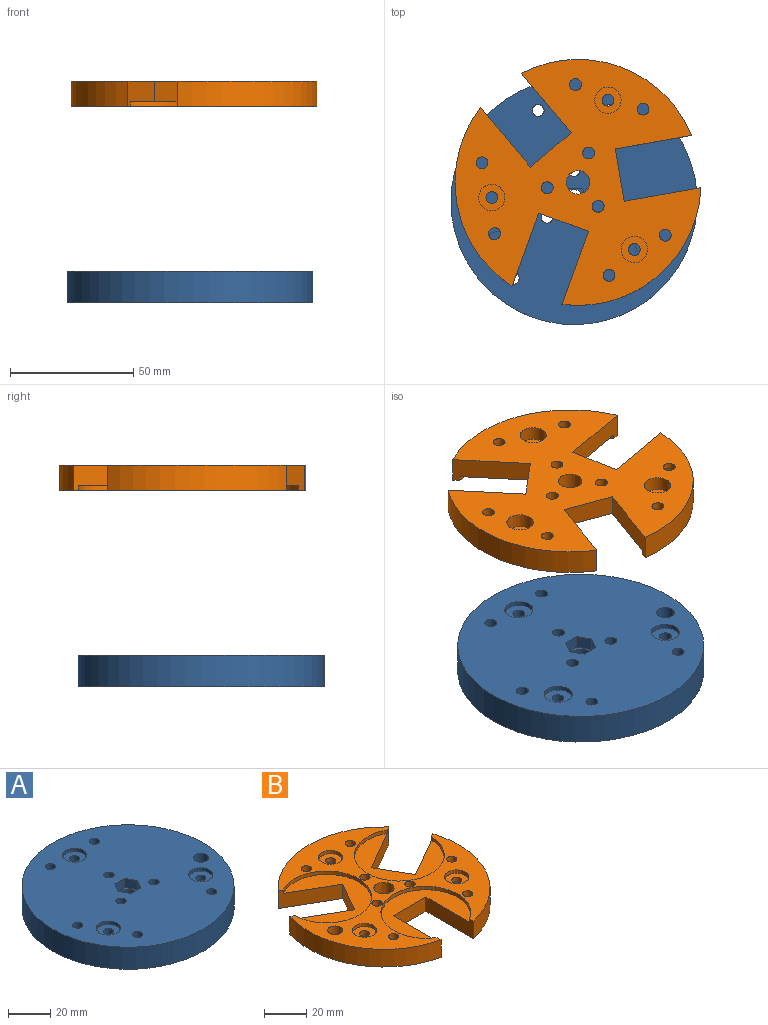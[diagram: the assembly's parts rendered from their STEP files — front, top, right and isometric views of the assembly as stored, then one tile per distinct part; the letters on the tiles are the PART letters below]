
ASSEMBLY  parts=2 mates=1
PART A: 29 faces, bbox 100x100x12.8 mm
  f0: cylinder r=4.76mm len=9.53mm, axis (0,0,-1), area 225.7mm2, adj f20,f28
  f1: plane 11.43x11.43mm, normal (0,0,1), area 84.8mm2, adj f4,f17
  f2: plane 11.43x11.43mm, normal (0,0,1), area 84.8mm2, adj f5,f16
  f3: plane 11.43x11.43mm, normal (0,0,1), area 84.8mm2, adj f6,f15
  f4: cylinder r=2.38mm len=10.8mm, axis (0,0,-1), area 161.5mm2, adj f1,f28
  f5: cylinder r=2.38mm len=10.8mm, axis (0,0,-1), area 161.5mm2, adj f2,f28
  f6: cylinder r=2.38mm len=10.8mm, axis (0,0,-1), area 161.5mm2, adj f3,f28
  f7: cylinder r=2.41mm len=12.75mm, axis (0,0,-1), area 193.3mm2, adj f18,f28
  f8: cylinder r=2.41mm len=12.75mm, axis (0,0,-1), area 193.3mm2, adj f18,f28
  f9: cylinder r=2.41mm len=12.75mm, axis (0,0,-1), area 193.3mm2, adj f18,f28
  f10: cylinder r=2.41mm len=12.75mm, axis (0,0,-1), area 193.3mm2, adj f18,f28
  f11: cylinder r=2.41mm len=12.75mm, axis (0,0,-1), area 193.3mm2, adj f18,f28
  f12: cylinder r=2.41mm len=12.75mm, axis (0,0,-1), area 193.3mm2, adj f18,f28
  f13: cylinder r=2.41mm len=12.75mm, axis (0,0,-1), area 193.3mm2, adj f18,f28
  f14: cylinder r=2.41mm len=12.75mm, axis (0,0,-1), area 193.3mm2, adj f18,f28
  f15: cylinder r=5.71mm len=11.43mm, axis (0,0,-1), area 70.2mm2, adj f3,f18
  f16: cylinder r=5.71mm len=11.43mm, axis (0,0,-1), area 70.2mm2, adj f2,f18
  f17: cylinder r=5.71mm len=11.43mm, axis (0,0,-1), area 70.2mm2, adj f1,f18
  f18: plane 100.03x100.03mm, normal (0,0,1), area 7258.8mm2, adj f7,f8,f9,f10,f11,f12,f13,f14
  f19: cylinder r=50.01mm len=100.03mm, axis (0,0,1), area 4006.8mm2, adj f18,f28
  f20: plane 12.73x11.02mm, normal (0,0,1), area 34mm2, adj f0,f21,f22,f23,f24,f25,f26
  f21: plane 6.36x5.21mm, normal (0,1,0), area 33.1mm2, adj f18,f20,f22,f26
  f22: plane 5.51x5.21mm, normal (-0.87,0.5,0), area 33.1mm2, adj f18,f20,f21,f23
  f23: plane 5.51x5.21mm, normal (-0.87,-0.5,0), area 33.1mm2, adj f18,f20,f22,f24
  f24: plane 6.36x5.21mm, normal (0,-1,0), area 33.1mm2, adj f18,f20,f23,f25
  f25: plane 5.51x5.21mm, normal (0.87,-0.5,0), area 33.1mm2, adj f18,f20,f24,f26
  f26: plane 5.51x5.21mm, normal (0.87,0.5,0), area 33.1mm2, adj f18,f20,f21,f25
  f27: cylinder r=3.56mm len=12.75mm, axis (0,0,1), area 284.9mm2, adj f18,f28
  f28: plane 100.03x100.03mm, normal (0,0,-1), area 7547.2mm2, adj f0,f4,f5,f6,f7,f8,f9,f10
PART B: 47 faces, bbox 100x98.8x10.2 mm
  f0: cylinder r=2.41mm len=4.83mm, axis (0,0,-1), area 39.3mm2, adj f23,f45
  f1: plane 42.42x39.47mm, normal (0,0,1), area 744.1mm2, adj f13,f14,f15,f38
  f2: plane 42.42x42.42mm, normal (0,0,1), area 744.1mm2, adj f16,f17,f18,f40
  f3: plane 42.42x42.42mm, normal (0,0,1), area 744.1mm2, adj f19,f20,f21,f39
  f4: plane 11.43x11.43mm, normal (0,0,1), area 84.8mm2, adj f7,f43
  f5: plane 11.43x11.43mm, normal (0,0,1), area 84.8mm2, adj f8,f42
  f6: plane 11.43x11.43mm, normal (0,0,1), area 84.8mm2, adj f9,f41
  f7: cylinder r=2.38mm len=4.76mm, axis (0,0,-1), area 36.1mm2, adj f4,f24
  f8: cylinder r=2.38mm len=4.76mm, axis (0,0,-1), area 36.1mm2, adj f5,f26
  f9: cylinder r=2.38mm len=4.76mm, axis (0,0,-1), area 36.1mm2, adj f6,f28
  f10: cylinder r=50mm len=73.77mm, axis (0,0,-1), area 847.1mm2, adj f18,f19,f23,f44
  f11: cylinder r=50mm len=63.88mm, axis (0,0,-1), area 847.1mm2, adj f15,f16,f23,f44
  f12: cylinder r=50mm len=63.88mm, axis (0,0,-1), area 847.1mm2, adj f13,f21,f23,f44
  f13: plane 31.62x10.21mm, normal (-1,0,0), area 266.1mm2, adj f1,f12,f14,f23,f38,f44
  f14: plane 21.59x8.26mm, normal (0,-1,0), area 178.2mm2, adj f1,f13,f15,f23
  f15: plane 31.62x10.21mm, normal (1,0,0), area 266.1mm2, adj f1,f11,f14,f23,f38,f44
  f16: plane 27.38x15.81mm, normal (0.5,0.87,0), area 266.1mm2, adj f2,f11,f17,f23,f40,f44
  f17: plane 18.7x10.8mm, normal (-0.87,0.5,0), area 178.2mm2, adj f2,f16,f18,f23
  f18: plane 27.38x15.81mm, normal (-0.5,-0.87,0), area 266.1mm2, adj f2,f10,f17,f23,f40,f44
  f19: plane 27.38x15.81mm, normal (0.5,-0.87,0), area 266.1mm2, adj f3,f10,f20,f23,f39,f44
  f20: plane 18.7x10.8mm, normal (0.87,0.5,0), area 178.2mm2, adj f3,f19,f21,f23
  f21: plane 27.38x15.81mm, normal (-0.5,0.87,0), area 266.1mm2, adj f3,f12,f20,f23,f39,f44
  f22: cylinder r=4.76mm len=10.21mm, axis (0,0,-1), area 305.5mm2, adj f23,f44
  f23: plane 100x98.82mm, normal (0,0,-1), area 5251.2mm2, adj f0,f10,f11,f12,f13,f14,f15,f16
  f24: plane 10.67x10.67mm, normal (0,0,-1), area 71.6mm2, adj f7,f25
  f25: cylinder r=5.33mm len=10.67mm, axis (0,0,-1), area 195.8mm2, adj f23,f24
  f26: plane 10.67x10.67mm, normal (0,0,-1), area 71.6mm2, adj f8,f27
  f27: cylinder r=5.33mm len=10.67mm, axis (0,0,-1), area 195.8mm2, adj f23,f26
  f28: plane 10.67x10.67mm, normal (0,0,-1), area 71.6mm2, adj f9,f29
  f29: cylinder r=5.33mm len=10.67mm, axis (0,0,-1), area 195.8mm2, adj f23,f28
  f30: cylinder r=2.41mm len=10.21mm, axis (0,0,-1), area 154.8mm2, adj f23,f44
  f31: cylinder r=2.41mm len=10.21mm, axis (0,0,-1), area 154.8mm2, adj f23,f44
  f32: cylinder r=2.41mm len=10.21mm, axis (0,0,-1), area 154.8mm2, adj f23,f44
  f33: cylinder r=2.41mm len=10.21mm, axis (0,0,-1), area 154.8mm2, adj f23,f44
  f34: cylinder r=2.41mm len=10.21mm, axis (0,0,-1), area 154.8mm2, adj f23,f44
  f35: cylinder r=2.41mm len=10.21mm, axis (0,0,-1), area 154.8mm2, adj f23,f44
  f36: cylinder r=2.41mm len=10.21mm, axis (0,0,-1), area 154.8mm2, adj f23,f44
  f37: cylinder r=2.41mm len=10.21mm, axis (0,0,-1), area 154.8mm2, adj f23,f44
  f38: cylinder r=21.21mm len=42.42mm, axis (0,0,-1), area 216.3mm2, adj f1,f13,f15,f44
  f39: cylinder r=21.21mm len=42.42mm, axis (0,0,-1), area 216.3mm2, adj f3,f19,f21,f44
  f40: cylinder r=21.21mm len=42.42mm, axis (0,0,-1), area 216.3mm2, adj f2,f16,f18,f44
  f41: cylinder r=5.71mm len=11.43mm, axis (0,0,-1), area 70.2mm2, adj f6,f44
  f42: cylinder r=5.71mm len=11.43mm, axis (0,0,-1), area 70.2mm2, adj f5,f44
  f43: cylinder r=5.71mm len=11.43mm, axis (0,0,-1), area 70.2mm2, adj f4,f44
  f44: plane 100x98.82mm, normal (0,0,1), area 2958.3mm2, adj f10,f11,f12,f13,f15,f16,f18,f19
  f45: plane 7.06x7.06mm, normal (0,0,1), area 20.9mm2, adj f0,f46
  f46: cylinder r=3.53mm len=7.62mm, axis (0,0,1), area 169mm2, adj f44,f45
PLACE A t=(-81.3,16.12,-59.69)mm
PLACE B rot(axis=(-0.17,-0.98,0),180deg) t=(-91.48,2.46,17.48)mm
MATE parallel B.f22 <-> A.f19  axis (0,0,1) through (-79.71,34.79,7.29)mm
